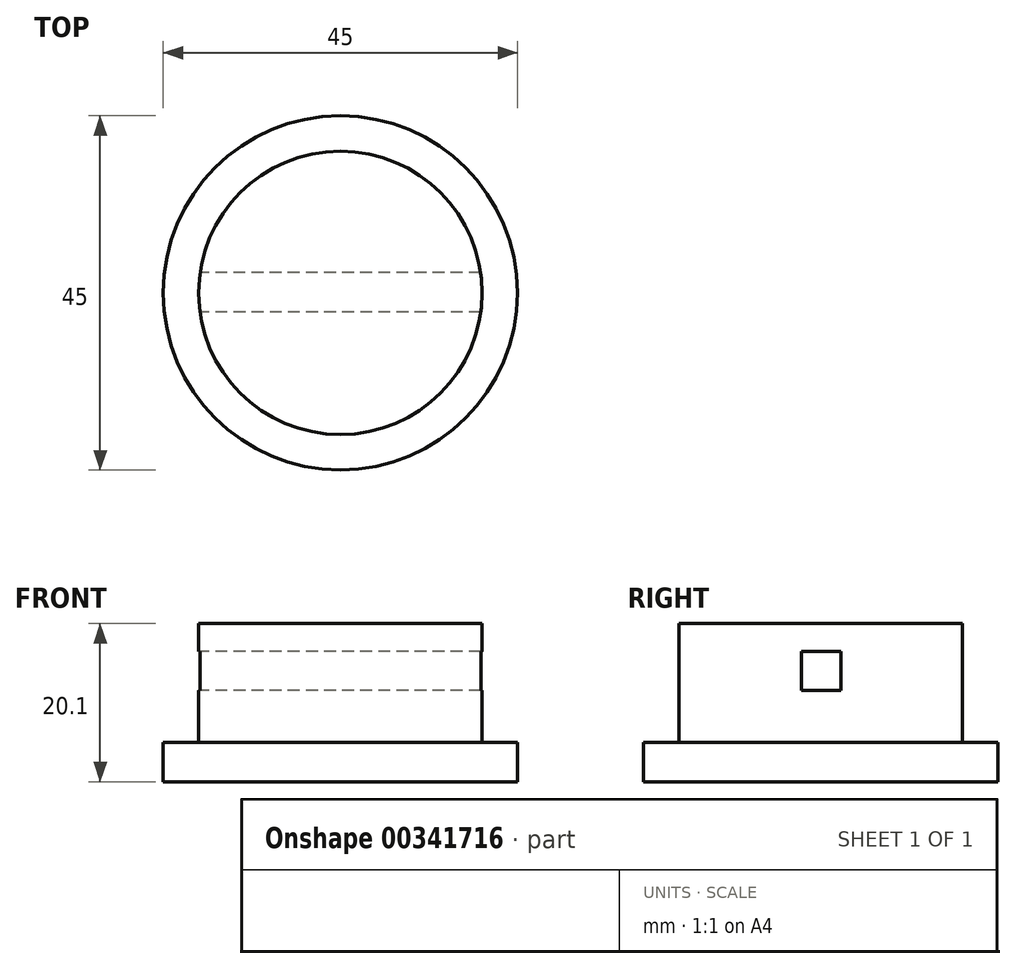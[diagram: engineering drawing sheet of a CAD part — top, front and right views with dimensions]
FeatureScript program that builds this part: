
annotation { "Feature Type Name" : "Feature", "Feature Type Description" : "" }
export const myFeature = defineFeature(function(context is Context, id is Id, definition is map)
    precondition{}
    {
        {
            var Q0;
            Q0=qCreatedBy(makeId("Top.planeOp"),FACE);
            var sketch = newSketch(context, id + "F0", { "sketchPlane" : qUnion([Q0])});
            skCircle(sketch, "E0", {"center": v(0, 0) * mm, "radius": 18 * mm});
            skCircle(sketch, "E1", {"center": v(0, 0) * mm, "radius": 22.5 * mm});
            skCircle(sketch, "E2", {"center": v(0, 0) * mm, "radius": 16 * mm});
            skSolve(sketch);
        }
        {
            var Q0;
            Q0=makeQuery(id+"F0.imprint","IMPRINT",FACE,{"disambiguationData":[TD([[makeQuery(id+"F0.imprint","IMPRINT",EDGE,{"derivedFrom":sQuery(id+"F0.wireOp",EDGE,"E2")}),1.0]])]});
            var Q1;
            Q1=makeQuery(id+"F0.imprint","IMPRINT",FACE,{"disambiguationData":[TD([[makeQuery(id+"F0.imprint","IMPRINT",EDGE,{"derivedFrom":sQuery(id+"F0.wireOp",EDGE,"E0")}),1.0]])]});
            extrude(context, id + "F1", {"entities" : qUnion([Q0, Q1]), "depth" : 20.1 * mm});
        }
        {
            var Q0;
            Q0=makeQuery(id+"F0.imprint","IMPRINT",FACE,{"disambiguationData":[TD([[makeQuery(id+"F0.imprint","IMPRINT",EDGE,{"derivedFrom":sQuery(id+"F0.wireOp",EDGE,"E0")}),-1.0]])]});
            extrude(context, id + "F2", {"entities" : qUnion([Q0]), "operationType" : NewBodyOperationType.ADD, "depth" : 5 * mm});
        }
        {
            var Q0;
            Q0=qCreatedBy(makeId("Right.planeOp"),FACE);
            var sketch = newSketch(context, id + "F3", { "sketchPlane" : qUnion([Q0])});
            skLineSegment(sketch, "E3.bottom", {"start": v(-2.44, 16.57) * mm, "end": v(2.56, 16.57) * mm});
            skLineSegment(sketch, "E3.top", {"start": v(-2.44, 11.57) * mm, "end": v(2.56, 11.57) * mm});
            skLineSegment(sketch, "E3.left", {"start": v(-2.44, 16.57) * mm, "end": v(-2.44, 11.57) * mm});
            skLineSegment(sketch, "E3.right", {"start": v(2.56, 16.57) * mm, "end": v(2.56, 11.57) * mm});
            skSolve(sketch);
        }
        {
            var Q0;
            Q0=makeQuery(id+"F3.imprint","IMPRINT",FACE,{"disambiguationData":[TD([[makeQuery(id+"F3.imprint","IMPRINT",EDGE,{"derivedFrom":sQuery(id+"F3.wireOp",EDGE,"E3.bottom")}),-1.0]])]});
            extrude(context, id + "F4", {"entities" : qUnion([Q0]), "operationType" : NewBodyOperationType.REMOVE, "depth" : 25 * mm, "hasSecondDirection" : true, "secondDirectionOppositeDirection" : true, "secondDirectionDepth" : 25 * mm});
        }
    });
